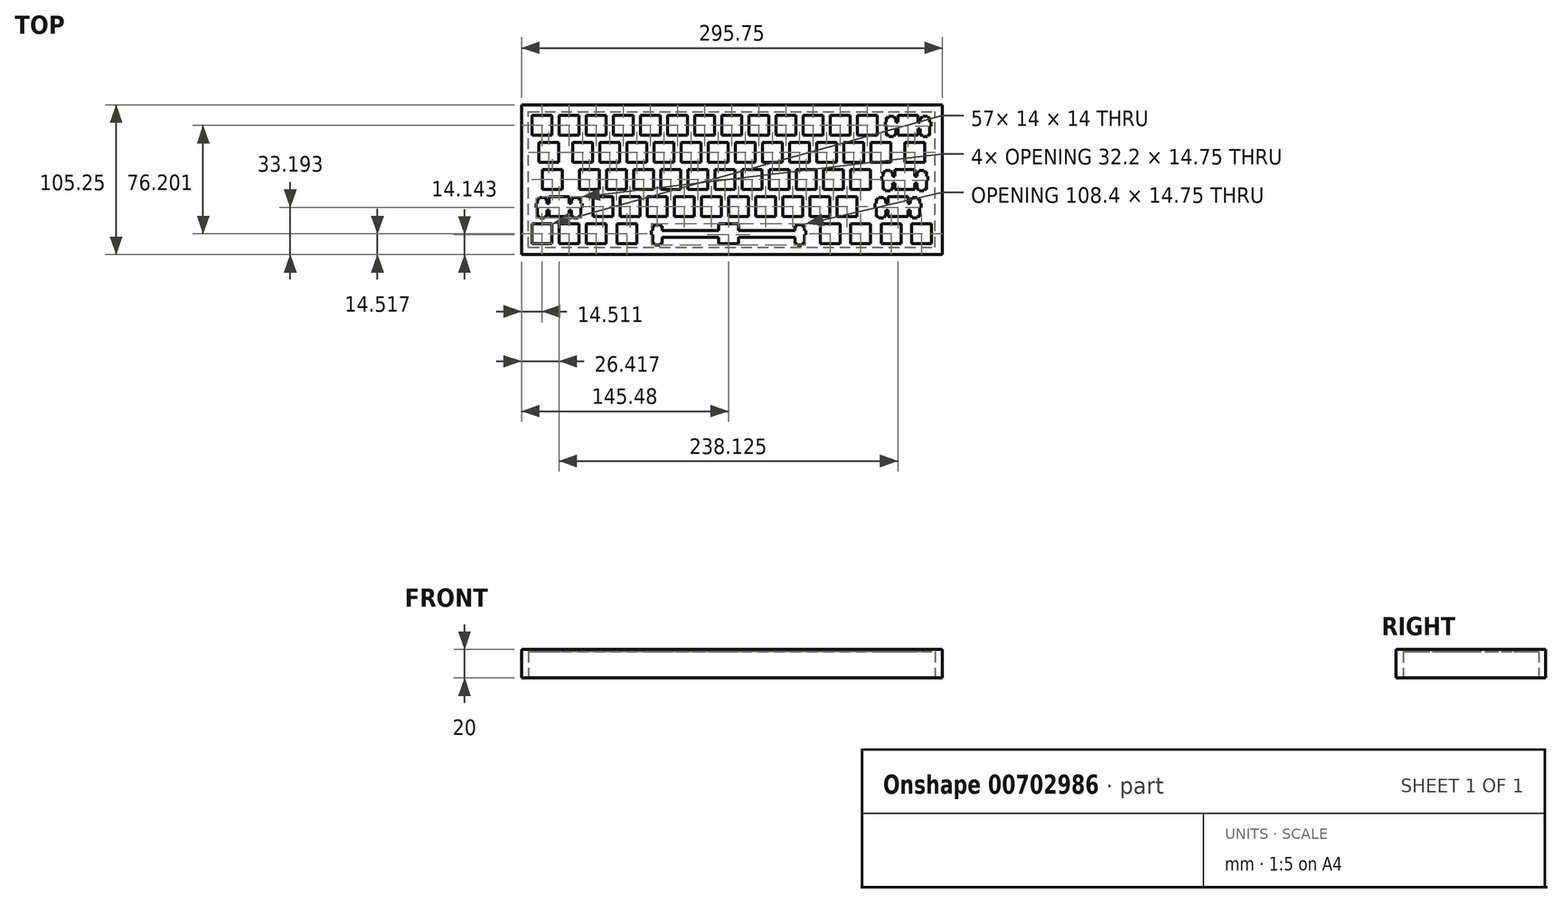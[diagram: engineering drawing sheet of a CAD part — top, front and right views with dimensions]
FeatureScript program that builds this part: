
annotation { "Feature Type Name" : "Feature", "Feature Type Description" : "" }
export const myFeature = defineFeature(function(context is Context, id is Id, definition is map)
    precondition{}
    {
        {
            var Q0;
            Q0=qCreatedBy(makeId("Top.planeOp"),FACE);
            var sketch = newSketch(context, id + "F0", { "sketchPlane" : qUnion([Q0])});
            skLineSegment(sketch, "E0.bottom", {"start": v(-142.74, 0) * mm, "end": v(153, 0) * mm});
            skLineSegment(sketch, "E0.top", {"start": v(-142.74, 105.25) * mm, "end": v(153, 105.25) * mm});
            skLineSegment(sketch, "E0.left", {"start": v(-142.74, 0) * mm, "end": v(-142.74, 105.25) * mm});
            skLineSegment(sketch, "E0.right", {"start": v(153, 0) * mm, "end": v(153, 105.25) * mm});
            skSolve(sketch);
        }
        {
            var Q0;
            Q0=makeQuery(id+"F0.imprint","IMPRINT",FACE,{"disambiguationData":[TD([[makeQuery(id+"F0.imprint","IMPRINT",EDGE,{"derivedFrom":sQuery(id+"F0.wireOp",EDGE,"E0.bottom")}),1.0]])]});
            extrude(context, id + "F1", {"entities" : qUnion([Q0]), "depth" : 20 * mm, "offsetDistance" : 25 * mm});
        }
        {
            var Q0;
            Q0=makeQuery(id+"F1.opExtrude","CAP_FACE",FACE,{"disambiguationData":[OSD([sQuery(id+"F0.wireOp",EDGE,"E0.bottom"),sQuery(id+"F0.wireOp",EDGE,"E0.top"),sQuery(id+"F0.wireOp",EDGE,"E0.left"),sQuery(id+"F0.wireOp",EDGE,"E0.right")])],"isStart":true});
            var sketch = newSketch(context, id + "F2", { "sketchPlane" : qUnion([Q0])});
            skLineSegment(sketch, "E1.bottom", {"start": v(-137.74, -5) * mm, "end": v(148, -5) * mm});
            skLineSegment(sketch, "E1.top", {"start": v(-137.74, -100.25) * mm, "end": v(148, -100.25) * mm});
            skLineSegment(sketch, "E1.left", {"start": v(-137.74, -5) * mm, "end": v(-137.74, -100.25) * mm});
            skLineSegment(sketch, "E1.right", {"start": v(148, -5) * mm, "end": v(148, -100.25) * mm});
            skSolve(sketch);
        }
        {
            var Q0;
            Q0=makeQuery(id+"F2.imprint","IMPRINT",FACE,{"disambiguationData":[TD([[makeQuery(id+"F2.imprint","IMPRINT",EDGE,{"derivedFrom":sQuery(id+"F2.wireOp",EDGE,"E1.bottom")}),-1.0]])]});
            extrude(context, id + "F3", {"entities" : qUnion([Q0]), "operationType" : NewBodyOperationType.REMOVE, "oppositeDirection" : true, "depth" : (20 - 1.54) * mm, "offsetDistance" : 25 * mm});
        }
        {
            var Q0;
            Q0=makeQuery(id+"F1.opExtrude","CAP_FACE",FACE,{"disambiguationData":[OSD([sQuery(id+"F0.wireOp",EDGE,"E0.bottom"),sQuery(id+"F0.wireOp",EDGE,"E0.top"),sQuery(id+"F0.wireOp",EDGE,"E0.left"),sQuery(id+"F0.wireOp",EDGE,"E0.right")])],"isStart":false});
            var sketch = newSketch(context, id + "F4", { "sketchPlane" : qUnion([Q0])});
            skLineSegment(sketch, "E2", {"start": v(-142.75, 105.24) * mm, "end": v(153, 105.24) * mm});
            skLineSegment(sketch, "E3", {"start": v(153, 105.24) * mm, "end": v(153, 0) * mm});
            skLineSegment(sketch, "E4", {"start": v(153, 0) * mm, "end": v(-142.75, 0) * mm});
            skLineSegment(sketch, "E5", {"start": v(-142.75, 0) * mm, "end": v(-142.75, 105.24) * mm});
            skLineSegment(sketch, "E6", {"start": v(-4.26, 21.52) * mm, "end": v(-4.26, 16.82) * mm});
            skLineSegment(sketch, "E7", {"start": v(-4.26, 16.82) * mm, "end": v(-43.88, 16.82) * mm});
            skLineSegment(sketch, "E8", {"start": v(-43.88, 16.82) * mm, "end": v(-43.88, 20.05) * mm});
            skLineSegment(sketch, "E9", {"start": v(-43.88, 20.05) * mm, "end": v(-45.6, 20.05) * mm});
            skLineSegment(sketch, "E10", {"start": v(-45.6, 20.05) * mm, "end": v(-45.6, 20.97) * mm});
            skLineSegment(sketch, "E11", {"start": v(-45.6, 20.97) * mm, "end": v(-48.91, 20.97) * mm});
            skLineSegment(sketch, "E12", {"start": v(-48.91, 20.97) * mm, "end": v(-48.91, 20.05) * mm});
            skLineSegment(sketch, "E13", {"start": v(-48.91, 20.05) * mm, "end": v(-50.64, 20.05) * mm});
            skLineSegment(sketch, "E14", {"start": v(-50.64, 20.05) * mm, "end": v(-50.64, 16.82) * mm});
            skLineSegment(sketch, "E15", {"start": v(-50.64, 16.82) * mm, "end": v(-51.46, 16.82) * mm});
            skLineSegment(sketch, "E16", {"start": v(-51.46, 16.82) * mm, "end": v(-51.46, 14.02) * mm});
            skLineSegment(sketch, "E17", {"start": v(-51.46, 14.02) * mm, "end": v(-50.64, 14.02) * mm});
            skLineSegment(sketch, "E18", {"start": v(-50.64, 14.02) * mm, "end": v(-50.64, 7.75) * mm});
            skLineSegment(sketch, "E19", {"start": v(-50.64, 7.75) * mm, "end": v(-48.91, 7.75) * mm});
            skLineSegment(sketch, "E20", {"start": v(-48.91, 7.75) * mm, "end": v(-48.91, 6.77) * mm});
            skLineSegment(sketch, "E21", {"start": v(-48.91, 6.77) * mm, "end": v(-45.6, 6.77) * mm});
            skLineSegment(sketch, "E22", {"start": v(-45.6, 6.77) * mm, "end": v(-45.6, 7.75) * mm});
            skLineSegment(sketch, "E23", {"start": v(-45.6, 7.75) * mm, "end": v(-43.88, 7.75) * mm});
            skLineSegment(sketch, "E24", {"start": v(-43.88, 7.75) * mm, "end": v(-43.88, 12.22) * mm});
            skLineSegment(sketch, "E25", {"start": v(-43.88, 12.22) * mm, "end": v(-4.26, 12.22) * mm});
            skLineSegment(sketch, "E26", {"start": v(-4.26, 12.22) * mm, "end": v(-4.26, 7.52) * mm});
            skLineSegment(sketch, "E27", {"start": v(-4.26, 7.52) * mm, "end": v(9.74, 7.52) * mm});
            skLineSegment(sketch, "E28", {"start": v(9.74, 7.52) * mm, "end": v(9.74, 12.22) * mm});
            skLineSegment(sketch, "E29", {"start": v(9.74, 12.22) * mm, "end": v(49.36, 12.22) * mm});
            skLineSegment(sketch, "E30", {"start": v(49.36, 12.22) * mm, "end": v(49.36, 7.75) * mm});
            skLineSegment(sketch, "E31", {"start": v(49.36, 7.75) * mm, "end": v(51.09, 7.75) * mm});
            skLineSegment(sketch, "E32", {"start": v(51.09, 7.75) * mm, "end": v(51.09, 6.77) * mm});
            skLineSegment(sketch, "E33", {"start": v(51.09, 6.77) * mm, "end": v(54.39, 6.77) * mm});
            skLineSegment(sketch, "E34", {"start": v(54.39, 6.77) * mm, "end": v(54.39, 7.75) * mm});
            skLineSegment(sketch, "E35", {"start": v(54.39, 7.75) * mm, "end": v(56.11, 7.75) * mm});
            skLineSegment(sketch, "E36", {"start": v(56.11, 7.75) * mm, "end": v(56.11, 14.02) * mm});
            skLineSegment(sketch, "E37", {"start": v(56.11, 14.02) * mm, "end": v(56.94, 14.02) * mm});
            skLineSegment(sketch, "E38", {"start": v(56.94, 14.02) * mm, "end": v(56.94, 16.82) * mm});
            skLineSegment(sketch, "E39", {"start": v(56.94, 16.82) * mm, "end": v(56.11, 16.82) * mm});
            skLineSegment(sketch, "E40", {"start": v(56.11, 16.82) * mm, "end": v(56.11, 20.05) * mm});
            skLineSegment(sketch, "E41", {"start": v(56.11, 20.05) * mm, "end": v(54.39, 20.05) * mm});
            skLineSegment(sketch, "E42", {"start": v(54.39, 20.05) * mm, "end": v(54.39, 20.97) * mm});
            skLineSegment(sketch, "E43", {"start": v(54.39, 20.97) * mm, "end": v(51.09, 20.97) * mm});
            skLineSegment(sketch, "E44", {"start": v(51.09, 20.97) * mm, "end": v(51.09, 20.05) * mm});
            skLineSegment(sketch, "E45", {"start": v(51.09, 20.05) * mm, "end": v(49.36, 20.05) * mm});
            skLineSegment(sketch, "E46", {"start": v(49.36, 20.05) * mm, "end": v(49.36, 16.82) * mm});
            skLineSegment(sketch, "E47", {"start": v(49.36, 16.82) * mm, "end": v(9.74, 16.82) * mm});
            skLineSegment(sketch, "E48", {"start": v(9.74, 16.82) * mm, "end": v(9.74, 21.52) * mm});
            skLineSegment(sketch, "E49", {"start": v(9.74, 21.52) * mm, "end": v(-4.26, 21.52) * mm});
            skLineSegment(sketch, "E50", {"start": v(-135.23, 21.52) * mm, "end": v(-121.23, 21.52) * mm});
            skLineSegment(sketch, "E51", {"start": v(-121.23, 21.52) * mm, "end": v(-121.23, 7.52) * mm});
            skLineSegment(sketch, "E52", {"start": v(-121.23, 7.52) * mm, "end": v(-135.23, 7.52) * mm});
            skLineSegment(sketch, "E53", {"start": v(-135.23, 7.52) * mm, "end": v(-135.23, 21.52) * mm});
            skLineSegment(sketch, "E54", {"start": v(-116.18, 21.52) * mm, "end": v(-102.18, 21.52) * mm});
            skLineSegment(sketch, "E55", {"start": v(-102.18, 21.52) * mm, "end": v(-102.18, 7.52) * mm});
            skLineSegment(sketch, "E56", {"start": v(-102.18, 7.52) * mm, "end": v(-116.18, 7.52) * mm});
            skLineSegment(sketch, "E57", {"start": v(-116.18, 7.52) * mm, "end": v(-116.18, 21.52) * mm});
            skLineSegment(sketch, "E58", {"start": v(-97.13, 21.52) * mm, "end": v(-83.13, 21.52) * mm});
            skLineSegment(sketch, "E59", {"start": v(-83.13, 21.52) * mm, "end": v(-83.13, 7.52) * mm});
            skLineSegment(sketch, "E60", {"start": v(-83.13, 7.52) * mm, "end": v(-97.13, 7.52) * mm});
            skLineSegment(sketch, "E61", {"start": v(-97.13, 7.52) * mm, "end": v(-97.13, 21.52) * mm});
            skLineSegment(sketch, "E62", {"start": v(-75.7, 21.52) * mm, "end": v(-61.7, 21.52) * mm});
            skLineSegment(sketch, "E63", {"start": v(-61.7, 21.52) * mm, "end": v(-61.7, 7.52) * mm});
            skLineSegment(sketch, "E64", {"start": v(-61.7, 7.52) * mm, "end": v(-75.7, 7.52) * mm});
            skLineSegment(sketch, "E65", {"start": v(-75.7, 7.52) * mm, "end": v(-75.7, 21.52) * mm});
            skLineSegment(sketch, "E66", {"start": v(67.18, 21.52) * mm, "end": v(81.18, 21.52) * mm});
            skLineSegment(sketch, "E67", {"start": v(81.18, 21.52) * mm, "end": v(81.18, 7.52) * mm});
            skLineSegment(sketch, "E68", {"start": v(81.18, 7.52) * mm, "end": v(67.18, 7.52) * mm});
            skLineSegment(sketch, "E69", {"start": v(67.18, 7.52) * mm, "end": v(67.18, 21.52) * mm});
            skLineSegment(sketch, "E70", {"start": v(88.6, 21.52) * mm, "end": v(102.6, 21.52) * mm});
            skLineSegment(sketch, "E71", {"start": v(102.6, 21.52) * mm, "end": v(102.6, 7.52) * mm});
            skLineSegment(sketch, "E72", {"start": v(102.6, 7.52) * mm, "end": v(88.6, 7.52) * mm});
            skLineSegment(sketch, "E73", {"start": v(88.6, 7.52) * mm, "end": v(88.6, 21.52) * mm});
            skLineSegment(sketch, "E74", {"start": v(110.04, 21.52) * mm, "end": v(124.04, 21.52) * mm});
            skLineSegment(sketch, "E75", {"start": v(124.04, 21.52) * mm, "end": v(124.04, 7.52) * mm});
            skLineSegment(sketch, "E76", {"start": v(124.04, 7.52) * mm, "end": v(110.04, 7.52) * mm});
            skLineSegment(sketch, "E77", {"start": v(110.04, 7.52) * mm, "end": v(110.04, 21.52) * mm});
            skLineSegment(sketch, "E78", {"start": v(131.47, 21.52) * mm, "end": v(145.47, 21.52) * mm});
            skLineSegment(sketch, "E79", {"start": v(145.47, 21.52) * mm, "end": v(145.47, 7.52) * mm});
            skLineSegment(sketch, "E80", {"start": v(145.47, 7.52) * mm, "end": v(131.47, 7.52) * mm});
            skLineSegment(sketch, "E81", {"start": v(131.47, 7.52) * mm, "end": v(131.47, 21.52) * mm});
            skLineSegment(sketch, "E82", {"start": v(-123.32, 40.57) * mm, "end": v(-123.32, 35.87) * mm});
            skLineSegment(sketch, "E83", {"start": v(-123.32, 35.87) * mm, "end": v(-124.85, 35.87) * mm});
            skLineSegment(sketch, "E84", {"start": v(-124.85, 35.87) * mm, "end": v(-124.85, 39.1) * mm});
            skLineSegment(sketch, "E85", {"start": v(-124.85, 39.1) * mm, "end": v(-126.57, 39.1) * mm});
            skLineSegment(sketch, "E86", {"start": v(-126.57, 39.1) * mm, "end": v(-126.57, 40.02) * mm});
            skLineSegment(sketch, "E87", {"start": v(-126.57, 40.02) * mm, "end": v(-129.87, 40.02) * mm});
            skLineSegment(sketch, "E88", {"start": v(-129.87, 40.02) * mm, "end": v(-129.87, 39.1) * mm});
            skLineSegment(sketch, "E89", {"start": v(-129.87, 39.1) * mm, "end": v(-131.6, 39.1) * mm});
            skLineSegment(sketch, "E90", {"start": v(-131.6, 39.1) * mm, "end": v(-131.6, 35.87) * mm});
            skLineSegment(sketch, "E91", {"start": v(-131.6, 35.87) * mm, "end": v(-132.42, 35.87) * mm});
            skLineSegment(sketch, "E92", {"start": v(-132.42, 35.87) * mm, "end": v(-132.42, 33.07) * mm});
            skLineSegment(sketch, "E93", {"start": v(-132.42, 33.07) * mm, "end": v(-131.6, 33.07) * mm});
            skLineSegment(sketch, "E94", {"start": v(-131.6, 33.07) * mm, "end": v(-131.6, 26.8) * mm});
            skLineSegment(sketch, "E95", {"start": v(-131.6, 26.8) * mm, "end": v(-129.87, 26.8) * mm});
            skLineSegment(sketch, "E96", {"start": v(-129.87, 26.8) * mm, "end": v(-129.87, 25.82) * mm});
            skLineSegment(sketch, "E97", {"start": v(-129.87, 25.82) * mm, "end": v(-126.57, 25.82) * mm});
            skLineSegment(sketch, "E98", {"start": v(-126.57, 25.82) * mm, "end": v(-126.57, 26.8) * mm});
            skLineSegment(sketch, "E99", {"start": v(-126.57, 26.8) * mm, "end": v(-124.85, 26.8) * mm});
            skLineSegment(sketch, "E100", {"start": v(-124.85, 26.8) * mm, "end": v(-124.85, 31.27) * mm});
            skLineSegment(sketch, "E101", {"start": v(-124.85, 31.27) * mm, "end": v(-123.32, 31.27) * mm});
            skLineSegment(sketch, "E102", {"start": v(-123.32, 31.27) * mm, "end": v(-123.32, 26.57) * mm});
            skLineSegment(sketch, "E103", {"start": v(-123.32, 26.57) * mm, "end": v(-109.32, 26.57) * mm});
            skLineSegment(sketch, "E104", {"start": v(-109.32, 26.57) * mm, "end": v(-109.32, 31.27) * mm});
            skLineSegment(sketch, "E105", {"start": v(-109.32, 31.27) * mm, "end": v(-107.8, 31.27) * mm});
            skLineSegment(sketch, "E106", {"start": v(-107.8, 31.27) * mm, "end": v(-107.8, 26.8) * mm});
            skLineSegment(sketch, "E107", {"start": v(-107.8, 26.8) * mm, "end": v(-106.07, 26.8) * mm});
            skLineSegment(sketch, "E108", {"start": v(-106.07, 26.8) * mm, "end": v(-106.07, 25.82) * mm});
            skLineSegment(sketch, "E109", {"start": v(-106.07, 25.82) * mm, "end": v(-102.77, 25.82) * mm});
            skLineSegment(sketch, "E110", {"start": v(-102.77, 25.82) * mm, "end": v(-102.77, 26.8) * mm});
            skLineSegment(sketch, "E111", {"start": v(-102.77, 26.8) * mm, "end": v(-101.05, 26.8) * mm});
            skLineSegment(sketch, "E112", {"start": v(-101.05, 26.8) * mm, "end": v(-101.05, 33.07) * mm});
            skLineSegment(sketch, "E113", {"start": v(-101.05, 33.07) * mm, "end": v(-100.22, 33.07) * mm});
            skLineSegment(sketch, "E114", {"start": v(-100.22, 33.07) * mm, "end": v(-100.22, 35.87) * mm});
            skLineSegment(sketch, "E115", {"start": v(-100.22, 35.87) * mm, "end": v(-101.05, 35.87) * mm});
            skLineSegment(sketch, "E116", {"start": v(-101.05, 35.87) * mm, "end": v(-101.05, 39.1) * mm});
            skLineSegment(sketch, "E117", {"start": v(-101.05, 39.1) * mm, "end": v(-102.77, 39.1) * mm});
            skLineSegment(sketch, "E118", {"start": v(-102.77, 39.1) * mm, "end": v(-102.77, 40.02) * mm});
            skLineSegment(sketch, "E119", {"start": v(-102.77, 40.02) * mm, "end": v(-106.07, 40.02) * mm});
            skLineSegment(sketch, "E120", {"start": v(-106.07, 40.02) * mm, "end": v(-106.07, 39.1) * mm});
            skLineSegment(sketch, "E121", {"start": v(-106.07, 39.1) * mm, "end": v(-107.8, 39.1) * mm});
            skLineSegment(sketch, "E122", {"start": v(-107.8, 39.1) * mm, "end": v(-107.8, 35.87) * mm});
            skLineSegment(sketch, "E123", {"start": v(-107.8, 35.87) * mm, "end": v(-109.32, 35.87) * mm});
            skLineSegment(sketch, "E124", {"start": v(-109.32, 35.87) * mm, "end": v(-109.32, 40.57) * mm});
            skLineSegment(sketch, "E125", {"start": v(-109.32, 40.57) * mm, "end": v(-123.32, 40.57) * mm});
            skLineSegment(sketch, "E126", {"start": v(114.8, 40.57) * mm, "end": v(114.8, 35.87) * mm});
            skLineSegment(sketch, "E127", {"start": v(114.8, 35.87) * mm, "end": v(113.28, 35.87) * mm});
            skLineSegment(sketch, "E128", {"start": v(113.28, 35.87) * mm, "end": v(113.28, 39.1) * mm});
            skLineSegment(sketch, "E129", {"start": v(113.28, 39.1) * mm, "end": v(111.55, 39.1) * mm});
            skLineSegment(sketch, "E130", {"start": v(111.55, 39.1) * mm, "end": v(111.55, 40.02) * mm});
            skLineSegment(sketch, "E131", {"start": v(111.55, 40.02) * mm, "end": v(108.25, 40.02) * mm});
            skLineSegment(sketch, "E132", {"start": v(108.25, 40.02) * mm, "end": v(108.25, 39.1) * mm});
            skLineSegment(sketch, "E133", {"start": v(108.25, 39.1) * mm, "end": v(106.53, 39.1) * mm});
            skLineSegment(sketch, "E134", {"start": v(106.53, 39.1) * mm, "end": v(106.53, 35.87) * mm});
            skLineSegment(sketch, "E135", {"start": v(106.53, 35.87) * mm, "end": v(105.7, 35.87) * mm});
            skLineSegment(sketch, "E136", {"start": v(105.7, 35.87) * mm, "end": v(105.7, 33.07) * mm});
            skLineSegment(sketch, "E137", {"start": v(105.7, 33.07) * mm, "end": v(106.53, 33.07) * mm});
            skLineSegment(sketch, "E138", {"start": v(106.53, 33.07) * mm, "end": v(106.53, 26.8) * mm});
            skLineSegment(sketch, "E139", {"start": v(106.53, 26.8) * mm, "end": v(108.25, 26.8) * mm});
            skLineSegment(sketch, "E140", {"start": v(108.25, 26.8) * mm, "end": v(108.25, 25.82) * mm});
            skLineSegment(sketch, "E141", {"start": v(108.25, 25.82) * mm, "end": v(111.55, 25.82) * mm});
            skLineSegment(sketch, "E142", {"start": v(111.55, 25.82) * mm, "end": v(111.55, 26.8) * mm});
            skLineSegment(sketch, "E143", {"start": v(111.55, 26.8) * mm, "end": v(113.28, 26.8) * mm});
            skLineSegment(sketch, "E144", {"start": v(113.28, 26.8) * mm, "end": v(113.28, 31.27) * mm});
            skLineSegment(sketch, "E145", {"start": v(113.28, 31.27) * mm, "end": v(114.8, 31.27) * mm});
            skLineSegment(sketch, "E146", {"start": v(114.8, 31.27) * mm, "end": v(114.8, 26.57) * mm});
            skLineSegment(sketch, "E147", {"start": v(114.8, 26.57) * mm, "end": v(128.8, 26.57) * mm});
            skLineSegment(sketch, "E148", {"start": v(128.8, 26.57) * mm, "end": v(128.8, 31.27) * mm});
            skLineSegment(sketch, "E149", {"start": v(128.8, 31.27) * mm, "end": v(130.33, 31.27) * mm});
            skLineSegment(sketch, "E150", {"start": v(130.33, 31.27) * mm, "end": v(130.33, 26.8) * mm});
            skLineSegment(sketch, "E151", {"start": v(130.33, 26.8) * mm, "end": v(132.05, 26.8) * mm});
            skLineSegment(sketch, "E152", {"start": v(132.05, 26.8) * mm, "end": v(132.05, 25.82) * mm});
            skLineSegment(sketch, "E153", {"start": v(132.05, 25.82) * mm, "end": v(135.35, 25.82) * mm});
            skLineSegment(sketch, "E154", {"start": v(135.35, 25.82) * mm, "end": v(135.35, 26.8) * mm});
            skLineSegment(sketch, "E155", {"start": v(135.35, 26.8) * mm, "end": v(137.08, 26.8) * mm});
            skLineSegment(sketch, "E156", {"start": v(137.08, 26.8) * mm, "end": v(137.08, 33.07) * mm});
            skLineSegment(sketch, "E157", {"start": v(137.08, 33.07) * mm, "end": v(137.9, 33.07) * mm});
            skLineSegment(sketch, "E158", {"start": v(137.9, 33.07) * mm, "end": v(137.9, 35.87) * mm});
            skLineSegment(sketch, "E159", {"start": v(137.9, 35.87) * mm, "end": v(137.08, 35.87) * mm});
            skLineSegment(sketch, "E160", {"start": v(137.08, 35.87) * mm, "end": v(137.08, 39.1) * mm});
            skLineSegment(sketch, "E161", {"start": v(137.08, 39.1) * mm, "end": v(135.35, 39.1) * mm});
            skLineSegment(sketch, "E162", {"start": v(135.35, 39.1) * mm, "end": v(135.35, 40.02) * mm});
            skLineSegment(sketch, "E163", {"start": v(135.35, 40.02) * mm, "end": v(132.05, 40.02) * mm});
            skLineSegment(sketch, "E164", {"start": v(132.05, 40.02) * mm, "end": v(132.05, 39.1) * mm});
            skLineSegment(sketch, "E165", {"start": v(132.05, 39.1) * mm, "end": v(130.33, 39.1) * mm});
            skLineSegment(sketch, "E166", {"start": v(130.33, 39.1) * mm, "end": v(130.33, 35.87) * mm});
            skLineSegment(sketch, "E167", {"start": v(130.33, 35.87) * mm, "end": v(128.8, 35.87) * mm});
            skLineSegment(sketch, "E168", {"start": v(128.8, 35.87) * mm, "end": v(128.8, 40.57) * mm});
            skLineSegment(sketch, "E169", {"start": v(128.8, 40.57) * mm, "end": v(114.8, 40.57) * mm});
            skLineSegment(sketch, "E170", {"start": v(-92.37, 40.57) * mm, "end": v(-78.37, 40.57) * mm});
            skLineSegment(sketch, "E171", {"start": v(-78.37, 40.57) * mm, "end": v(-78.37, 26.57) * mm});
            skLineSegment(sketch, "E172", {"start": v(-78.37, 26.57) * mm, "end": v(-92.37, 26.57) * mm});
            skLineSegment(sketch, "E173", {"start": v(-92.37, 26.57) * mm, "end": v(-92.37, 40.57) * mm});
            skLineSegment(sketch, "E174", {"start": v(-73.32, 40.57) * mm, "end": v(-59.32, 40.57) * mm});
            skLineSegment(sketch, "E175", {"start": v(-59.32, 40.57) * mm, "end": v(-59.32, 26.57) * mm});
            skLineSegment(sketch, "E176", {"start": v(-59.32, 26.57) * mm, "end": v(-73.32, 26.57) * mm});
            skLineSegment(sketch, "E177", {"start": v(-73.32, 26.57) * mm, "end": v(-73.32, 40.57) * mm});
            skLineSegment(sketch, "E178", {"start": v(-54.27, 40.57) * mm, "end": v(-40.27, 40.57) * mm});
            skLineSegment(sketch, "E179", {"start": v(-40.27, 40.57) * mm, "end": v(-40.27, 26.57) * mm});
            skLineSegment(sketch, "E180", {"start": v(-40.27, 26.57) * mm, "end": v(-54.27, 26.57) * mm});
            skLineSegment(sketch, "E181", {"start": v(-54.27, 26.57) * mm, "end": v(-54.27, 40.57) * mm});
            skLineSegment(sketch, "E182", {"start": v(-35.22, 40.57) * mm, "end": v(-21.22, 40.57) * mm});
            skLineSegment(sketch, "E183", {"start": v(-21.22, 40.57) * mm, "end": v(-21.22, 26.57) * mm});
            skLineSegment(sketch, "E184", {"start": v(-21.22, 26.57) * mm, "end": v(-35.22, 26.57) * mm});
            skLineSegment(sketch, "E185", {"start": v(-35.22, 26.57) * mm, "end": v(-35.22, 40.57) * mm});
            skLineSegment(sketch, "E186", {"start": v(-16.17, 40.57) * mm, "end": v(-2.17, 40.57) * mm});
            skLineSegment(sketch, "E187", {"start": v(-2.17, 40.57) * mm, "end": v(-2.17, 26.57) * mm});
            skLineSegment(sketch, "E188", {"start": v(-2.17, 26.57) * mm, "end": v(-16.17, 26.57) * mm});
            skLineSegment(sketch, "E189", {"start": v(-16.17, 26.57) * mm, "end": v(-16.17, 40.57) * mm});
            skLineSegment(sketch, "E190", {"start": v(2.88, 40.57) * mm, "end": v(16.88, 40.57) * mm});
            skLineSegment(sketch, "E191", {"start": v(16.88, 40.57) * mm, "end": v(16.88, 26.57) * mm});
            skLineSegment(sketch, "E192", {"start": v(16.88, 26.57) * mm, "end": v(2.88, 26.57) * mm});
            skLineSegment(sketch, "E193", {"start": v(2.88, 26.57) * mm, "end": v(2.88, 40.57) * mm});
            skLineSegment(sketch, "E194", {"start": v(21.93, 40.57) * mm, "end": v(35.93, 40.57) * mm});
            skLineSegment(sketch, "E195", {"start": v(35.93, 40.57) * mm, "end": v(35.93, 26.57) * mm});
            skLineSegment(sketch, "E196", {"start": v(35.93, 26.57) * mm, "end": v(21.93, 26.57) * mm});
            skLineSegment(sketch, "E197", {"start": v(21.93, 26.57) * mm, "end": v(21.93, 40.57) * mm});
            skLineSegment(sketch, "E198", {"start": v(40.98, 40.57) * mm, "end": v(54.98, 40.57) * mm});
            skLineSegment(sketch, "E199", {"start": v(54.98, 40.57) * mm, "end": v(54.98, 26.57) * mm});
            skLineSegment(sketch, "E200", {"start": v(54.98, 26.57) * mm, "end": v(40.98, 26.57) * mm});
            skLineSegment(sketch, "E201", {"start": v(40.98, 26.57) * mm, "end": v(40.98, 40.57) * mm});
            skLineSegment(sketch, "E202", {"start": v(60.03, 40.57) * mm, "end": v(74.03, 40.57) * mm});
            skLineSegment(sketch, "E203", {"start": v(74.03, 40.57) * mm, "end": v(74.03, 26.57) * mm});
            skLineSegment(sketch, "E204", {"start": v(74.03, 26.57) * mm, "end": v(60.03, 26.57) * mm});
            skLineSegment(sketch, "E205", {"start": v(60.03, 26.57) * mm, "end": v(60.03, 40.57) * mm});
            skLineSegment(sketch, "E206", {"start": v(79.08, 40.57) * mm, "end": v(93.08, 40.57) * mm});
            skLineSegment(sketch, "E207", {"start": v(93.08, 40.57) * mm, "end": v(93.08, 26.57) * mm});
            skLineSegment(sketch, "E208", {"start": v(93.08, 26.57) * mm, "end": v(79.08, 26.57) * mm});
            skLineSegment(sketch, "E209", {"start": v(79.08, 26.57) * mm, "end": v(79.08, 40.57) * mm});
            skLineSegment(sketch, "E210", {"start": v(119.56, 59.62) * mm, "end": v(119.56, 54.92) * mm});
            skLineSegment(sketch, "E211", {"start": v(119.56, 54.92) * mm, "end": v(118.04, 54.92) * mm});
            skLineSegment(sketch, "E212", {"start": v(118.04, 54.92) * mm, "end": v(118.04, 58.15) * mm});
            skLineSegment(sketch, "E213", {"start": v(118.04, 58.15) * mm, "end": v(116.31, 58.15) * mm});
            skLineSegment(sketch, "E214", {"start": v(116.31, 58.15) * mm, "end": v(116.31, 59.07) * mm});
            skLineSegment(sketch, "E215", {"start": v(116.31, 59.07) * mm, "end": v(113.01, 59.07) * mm});
            skLineSegment(sketch, "E216", {"start": v(113.01, 59.07) * mm, "end": v(113.01, 58.15) * mm});
            skLineSegment(sketch, "E217", {"start": v(113.01, 58.15) * mm, "end": v(111.29, 58.15) * mm});
            skLineSegment(sketch, "E218", {"start": v(111.29, 58.15) * mm, "end": v(111.29, 54.92) * mm});
            skLineSegment(sketch, "E219", {"start": v(111.29, 54.92) * mm, "end": v(110.46, 54.92) * mm});
            skLineSegment(sketch, "E220", {"start": v(110.46, 54.92) * mm, "end": v(110.46, 52.12) * mm});
            skLineSegment(sketch, "E221", {"start": v(110.46, 52.12) * mm, "end": v(111.29, 52.12) * mm});
            skLineSegment(sketch, "E222", {"start": v(111.29, 52.12) * mm, "end": v(111.29, 45.85) * mm});
            skLineSegment(sketch, "E223", {"start": v(111.29, 45.85) * mm, "end": v(113.01, 45.85) * mm});
            skLineSegment(sketch, "E224", {"start": v(113.01, 45.85) * mm, "end": v(113.01, 44.87) * mm});
            skLineSegment(sketch, "E225", {"start": v(113.01, 44.87) * mm, "end": v(116.31, 44.87) * mm});
            skLineSegment(sketch, "E226", {"start": v(116.31, 44.87) * mm, "end": v(116.31, 45.85) * mm});
            skLineSegment(sketch, "E227", {"start": v(116.31, 45.85) * mm, "end": v(118.04, 45.85) * mm});
            skLineSegment(sketch, "E228", {"start": v(118.04, 45.85) * mm, "end": v(118.04, 50.32) * mm});
            skLineSegment(sketch, "E229", {"start": v(118.04, 50.32) * mm, "end": v(119.56, 50.32) * mm});
            skLineSegment(sketch, "E230", {"start": v(119.56, 50.32) * mm, "end": v(119.56, 45.62) * mm});
            skLineSegment(sketch, "E231", {"start": v(119.56, 45.62) * mm, "end": v(133.56, 45.62) * mm});
            skLineSegment(sketch, "E232", {"start": v(133.56, 45.62) * mm, "end": v(133.56, 50.32) * mm});
            skLineSegment(sketch, "E233", {"start": v(133.56, 50.32) * mm, "end": v(135.09, 50.32) * mm});
            skLineSegment(sketch, "E234", {"start": v(135.09, 50.32) * mm, "end": v(135.09, 45.85) * mm});
            skLineSegment(sketch, "E235", {"start": v(135.09, 45.85) * mm, "end": v(136.81, 45.85) * mm});
            skLineSegment(sketch, "E236", {"start": v(136.81, 45.85) * mm, "end": v(136.81, 44.87) * mm});
            skLineSegment(sketch, "E237", {"start": v(136.81, 44.87) * mm, "end": v(140.11, 44.87) * mm});
            skLineSegment(sketch, "E238", {"start": v(140.11, 44.87) * mm, "end": v(140.11, 45.85) * mm});
            skLineSegment(sketch, "E239", {"start": v(140.11, 45.85) * mm, "end": v(141.84, 45.85) * mm});
            skLineSegment(sketch, "E240", {"start": v(141.84, 45.85) * mm, "end": v(141.84, 52.12) * mm});
            skLineSegment(sketch, "E241", {"start": v(141.84, 52.12) * mm, "end": v(142.66, 52.12) * mm});
            skLineSegment(sketch, "E242", {"start": v(142.66, 52.12) * mm, "end": v(142.66, 54.92) * mm});
            skLineSegment(sketch, "E243", {"start": v(142.66, 54.92) * mm, "end": v(141.84, 54.92) * mm});
            skLineSegment(sketch, "E244", {"start": v(141.84, 54.92) * mm, "end": v(141.84, 58.15) * mm});
            skLineSegment(sketch, "E245", {"start": v(141.84, 58.15) * mm, "end": v(140.11, 58.15) * mm});
            skLineSegment(sketch, "E246", {"start": v(140.11, 58.15) * mm, "end": v(140.11, 59.07) * mm});
            skLineSegment(sketch, "E247", {"start": v(140.11, 59.07) * mm, "end": v(136.81, 59.07) * mm});
            skLineSegment(sketch, "E248", {"start": v(136.81, 59.07) * mm, "end": v(136.81, 58.15) * mm});
            skLineSegment(sketch, "E249", {"start": v(136.81, 58.15) * mm, "end": v(135.09, 58.15) * mm});
            skLineSegment(sketch, "E250", {"start": v(135.09, 58.15) * mm, "end": v(135.09, 54.92) * mm});
            skLineSegment(sketch, "E251", {"start": v(135.09, 54.92) * mm, "end": v(133.56, 54.92) * mm});
            skLineSegment(sketch, "E252", {"start": v(133.56, 54.92) * mm, "end": v(133.56, 59.62) * mm});
            skLineSegment(sketch, "E253", {"start": v(133.56, 59.62) * mm, "end": v(119.56, 59.62) * mm});
            skLineSegment(sketch, "E254", {"start": v(-128.09, 59.62) * mm, "end": v(-114.08, 59.62) * mm});
            skLineSegment(sketch, "E255", {"start": v(-114.08, 59.62) * mm, "end": v(-114.08, 45.62) * mm});
            skLineSegment(sketch, "E256", {"start": v(-114.08, 45.62) * mm, "end": v(-128.09, 45.62) * mm});
            skLineSegment(sketch, "E257", {"start": v(-128.09, 45.62) * mm, "end": v(-128.09, 59.62) * mm});
            skLineSegment(sketch, "E258", {"start": v(-101.9, 59.62) * mm, "end": v(-87.9, 59.62) * mm});
            skLineSegment(sketch, "E259", {"start": v(-87.9, 59.62) * mm, "end": v(-87.9, 45.62) * mm});
            skLineSegment(sketch, "E260", {"start": v(-87.9, 45.62) * mm, "end": v(-101.9, 45.62) * mm});
            skLineSegment(sketch, "E261", {"start": v(-101.9, 45.62) * mm, "end": v(-101.9, 59.62) * mm});
            skLineSegment(sketch, "E262", {"start": v(-82.84, 59.62) * mm, "end": v(-68.84, 59.62) * mm});
            skLineSegment(sketch, "E263", {"start": v(-68.84, 59.62) * mm, "end": v(-68.84, 45.62) * mm});
            skLineSegment(sketch, "E264", {"start": v(-68.84, 45.62) * mm, "end": v(-82.84, 45.62) * mm});
            skLineSegment(sketch, "E265", {"start": v(-82.84, 45.62) * mm, "end": v(-82.84, 59.62) * mm});
            skLineSegment(sketch, "E266", {"start": v(-63.8, 59.62) * mm, "end": v(-49.8, 59.62) * mm});
            skLineSegment(sketch, "E267", {"start": v(-49.8, 59.62) * mm, "end": v(-49.8, 45.62) * mm});
            skLineSegment(sketch, "E268", {"start": v(-49.8, 45.62) * mm, "end": v(-63.8, 45.62) * mm});
            skLineSegment(sketch, "E269", {"start": v(-63.8, 45.62) * mm, "end": v(-63.8, 59.62) * mm});
            skLineSegment(sketch, "E270", {"start": v(-44.74, 59.62) * mm, "end": v(-30.74, 59.62) * mm});
            skLineSegment(sketch, "E271", {"start": v(-30.74, 59.62) * mm, "end": v(-30.74, 45.62) * mm});
            skLineSegment(sketch, "E272", {"start": v(-30.74, 45.62) * mm, "end": v(-44.74, 45.62) * mm});
            skLineSegment(sketch, "E273", {"start": v(-44.74, 45.62) * mm, "end": v(-44.74, 59.62) * mm});
            skLineSegment(sketch, "E274", {"start": v(-25.7, 59.62) * mm, "end": v(-11.7, 59.62) * mm});
            skLineSegment(sketch, "E275", {"start": v(-11.7, 59.62) * mm, "end": v(-11.7, 45.62) * mm});
            skLineSegment(sketch, "E276", {"start": v(-11.7, 45.62) * mm, "end": v(-25.7, 45.62) * mm});
            skLineSegment(sketch, "E277", {"start": v(-25.7, 45.62) * mm, "end": v(-25.7, 59.62) * mm});
            skLineSegment(sketch, "E278", {"start": v(-6.64, 59.62) * mm, "end": v(7.36, 59.62) * mm});
            skLineSegment(sketch, "E279", {"start": v(7.36, 59.62) * mm, "end": v(7.36, 45.62) * mm});
            skLineSegment(sketch, "E280", {"start": v(7.36, 45.62) * mm, "end": v(-6.64, 45.62) * mm});
            skLineSegment(sketch, "E281", {"start": v(-6.64, 45.62) * mm, "end": v(-6.64, 59.62) * mm});
            skLineSegment(sketch, "E282", {"start": v(12.4, 59.62) * mm, "end": v(26.4, 59.62) * mm});
            skLineSegment(sketch, "E283", {"start": v(26.4, 59.62) * mm, "end": v(26.4, 45.62) * mm});
            skLineSegment(sketch, "E284", {"start": v(26.4, 45.62) * mm, "end": v(12.4, 45.62) * mm});
            skLineSegment(sketch, "E285", {"start": v(12.4, 45.62) * mm, "end": v(12.4, 59.62) * mm});
            skLineSegment(sketch, "E286", {"start": v(31.46, 59.62) * mm, "end": v(45.46, 59.62) * mm});
            skLineSegment(sketch, "E287", {"start": v(45.46, 59.62) * mm, "end": v(45.46, 45.62) * mm});
            skLineSegment(sketch, "E288", {"start": v(45.46, 45.62) * mm, "end": v(31.46, 45.62) * mm});
            skLineSegment(sketch, "E289", {"start": v(31.46, 45.62) * mm, "end": v(31.46, 59.62) * mm});
            skLineSegment(sketch, "E290", {"start": v(50.5, 59.62) * mm, "end": v(64.5, 59.62) * mm});
            skLineSegment(sketch, "E291", {"start": v(64.5, 59.62) * mm, "end": v(64.5, 45.62) * mm});
            skLineSegment(sketch, "E292", {"start": v(64.5, 45.62) * mm, "end": v(50.5, 45.62) * mm});
            skLineSegment(sketch, "E293", {"start": v(50.5, 45.62) * mm, "end": v(50.5, 59.62) * mm});
            skLineSegment(sketch, "E294", {"start": v(69.56, 59.62) * mm, "end": v(83.56, 59.62) * mm});
            skLineSegment(sketch, "E295", {"start": v(83.56, 59.62) * mm, "end": v(83.56, 45.62) * mm});
            skLineSegment(sketch, "E296", {"start": v(83.56, 45.62) * mm, "end": v(69.56, 45.62) * mm});
            skLineSegment(sketch, "E297", {"start": v(69.56, 45.62) * mm, "end": v(69.56, 59.62) * mm});
            skLineSegment(sketch, "E298", {"start": v(88.6, 59.62) * mm, "end": v(102.6, 59.62) * mm});
            skLineSegment(sketch, "E299", {"start": v(102.6, 59.62) * mm, "end": v(102.6, 45.62) * mm});
            skLineSegment(sketch, "E300", {"start": v(102.6, 45.62) * mm, "end": v(88.6, 45.62) * mm});
            skLineSegment(sketch, "E301", {"start": v(88.6, 45.62) * mm, "end": v(88.6, 59.62) * mm});
            skLineSegment(sketch, "E302", {"start": v(-130.47, 78.67) * mm, "end": v(-116.47, 78.67) * mm});
            skLineSegment(sketch, "E303", {"start": v(-116.47, 78.67) * mm, "end": v(-116.47, 64.67) * mm});
            skLineSegment(sketch, "E304", {"start": v(-116.47, 64.67) * mm, "end": v(-130.47, 64.67) * mm});
            skLineSegment(sketch, "E305", {"start": v(-130.47, 64.67) * mm, "end": v(-130.47, 78.67) * mm});
            skLineSegment(sketch, "E306", {"start": v(-106.65, 78.67) * mm, "end": v(-92.65, 78.67) * mm});
            skLineSegment(sketch, "E307", {"start": v(-92.65, 78.67) * mm, "end": v(-92.65, 64.67) * mm});
            skLineSegment(sketch, "E308", {"start": v(-92.65, 64.67) * mm, "end": v(-106.65, 64.67) * mm});
            skLineSegment(sketch, "E309", {"start": v(-106.65, 64.67) * mm, "end": v(-106.65, 78.67) * mm});
            skLineSegment(sketch, "E310", {"start": v(-87.6, 78.67) * mm, "end": v(-73.6, 78.67) * mm});
            skLineSegment(sketch, "E311", {"start": v(-73.6, 78.67) * mm, "end": v(-73.6, 64.67) * mm});
            skLineSegment(sketch, "E312", {"start": v(-73.6, 64.67) * mm, "end": v(-87.6, 64.67) * mm});
            skLineSegment(sketch, "E313", {"start": v(-87.6, 64.67) * mm, "end": v(-87.6, 78.67) * mm});
            skLineSegment(sketch, "E314", {"start": v(-68.55, 78.67) * mm, "end": v(-54.55, 78.67) * mm});
            skLineSegment(sketch, "E315", {"start": v(-54.55, 78.67) * mm, "end": v(-54.55, 64.67) * mm});
            skLineSegment(sketch, "E316", {"start": v(-54.55, 64.67) * mm, "end": v(-68.55, 64.67) * mm});
            skLineSegment(sketch, "E317", {"start": v(-68.55, 64.67) * mm, "end": v(-68.55, 78.67) * mm});
            skLineSegment(sketch, "E318", {"start": v(-49.5, 78.67) * mm, "end": v(-35.5, 78.67) * mm});
            skLineSegment(sketch, "E319", {"start": v(-35.5, 78.67) * mm, "end": v(-35.5, 64.67) * mm});
            skLineSegment(sketch, "E320", {"start": v(-35.5, 64.67) * mm, "end": v(-49.5, 64.67) * mm});
            skLineSegment(sketch, "E321", {"start": v(-49.5, 64.67) * mm, "end": v(-49.5, 78.67) * mm});
            skLineSegment(sketch, "E322", {"start": v(-30.45, 78.67) * mm, "end": v(-16.45, 78.67) * mm});
            skLineSegment(sketch, "E323", {"start": v(-16.45, 78.67) * mm, "end": v(-16.45, 64.67) * mm});
            skLineSegment(sketch, "E324", {"start": v(-16.45, 64.67) * mm, "end": v(-30.45, 64.67) * mm});
            skLineSegment(sketch, "E325", {"start": v(-30.45, 64.67) * mm, "end": v(-30.45, 78.67) * mm});
            skLineSegment(sketch, "E326", {"start": v(-11.4, 78.67) * mm, "end": v(2.6, 78.67) * mm});
            skLineSegment(sketch, "E327", {"start": v(2.6, 78.67) * mm, "end": v(2.6, 64.67) * mm});
            skLineSegment(sketch, "E328", {"start": v(2.6, 64.67) * mm, "end": v(-11.4, 64.67) * mm});
            skLineSegment(sketch, "E329", {"start": v(-11.4, 64.67) * mm, "end": v(-11.4, 78.67) * mm});
            skLineSegment(sketch, "E330", {"start": v(7.65, 78.67) * mm, "end": v(21.65, 78.67) * mm});
            skLineSegment(sketch, "E331", {"start": v(21.65, 78.67) * mm, "end": v(21.65, 64.67) * mm});
            skLineSegment(sketch, "E332", {"start": v(21.65, 64.67) * mm, "end": v(7.65, 64.67) * mm});
            skLineSegment(sketch, "E333", {"start": v(7.65, 64.67) * mm, "end": v(7.65, 78.67) * mm});
            skLineSegment(sketch, "E334", {"start": v(26.7, 78.67) * mm, "end": v(40.7, 78.67) * mm});
            skLineSegment(sketch, "E335", {"start": v(40.7, 78.67) * mm, "end": v(40.7, 64.67) * mm});
            skLineSegment(sketch, "E336", {"start": v(40.7, 64.67) * mm, "end": v(26.7, 64.67) * mm});
            skLineSegment(sketch, "E337", {"start": v(26.7, 64.67) * mm, "end": v(26.7, 78.67) * mm});
            skLineSegment(sketch, "E338", {"start": v(45.75, 78.67) * mm, "end": v(59.75, 78.67) * mm});
            skLineSegment(sketch, "E339", {"start": v(59.75, 78.67) * mm, "end": v(59.75, 64.67) * mm});
            skLineSegment(sketch, "E340", {"start": v(59.75, 64.67) * mm, "end": v(45.75, 64.67) * mm});
            skLineSegment(sketch, "E341", {"start": v(45.75, 64.67) * mm, "end": v(45.75, 78.67) * mm});
            skLineSegment(sketch, "E342", {"start": v(64.8, 78.67) * mm, "end": v(78.8, 78.67) * mm});
            skLineSegment(sketch, "E343", {"start": v(78.8, 78.67) * mm, "end": v(78.8, 64.67) * mm});
            skLineSegment(sketch, "E344", {"start": v(78.8, 64.67) * mm, "end": v(64.8, 64.67) * mm});
            skLineSegment(sketch, "E345", {"start": v(64.8, 64.67) * mm, "end": v(64.8, 78.67) * mm});
            skLineSegment(sketch, "E346", {"start": v(83.85, 78.67) * mm, "end": v(97.85, 78.67) * mm});
            skLineSegment(sketch, "E347", {"start": v(97.85, 78.67) * mm, "end": v(97.85, 64.67) * mm});
            skLineSegment(sketch, "E348", {"start": v(97.85, 64.67) * mm, "end": v(83.85, 64.67) * mm});
            skLineSegment(sketch, "E349", {"start": v(83.85, 64.67) * mm, "end": v(83.85, 78.67) * mm});
            skLineSegment(sketch, "E350", {"start": v(102.9, 78.67) * mm, "end": v(116.9, 78.67) * mm});
            skLineSegment(sketch, "E351", {"start": v(116.9, 78.67) * mm, "end": v(116.9, 64.67) * mm});
            skLineSegment(sketch, "E352", {"start": v(116.9, 64.67) * mm, "end": v(102.9, 64.67) * mm});
            skLineSegment(sketch, "E353", {"start": v(102.9, 64.67) * mm, "end": v(102.9, 78.67) * mm});
            skLineSegment(sketch, "E354", {"start": v(126.7, 78.67) * mm, "end": v(140.7, 78.67) * mm});
            skLineSegment(sketch, "E355", {"start": v(140.7, 78.67) * mm, "end": v(140.7, 64.67) * mm});
            skLineSegment(sketch, "E356", {"start": v(140.7, 64.67) * mm, "end": v(126.7, 64.67) * mm});
            skLineSegment(sketch, "E357", {"start": v(126.7, 64.67) * mm, "end": v(126.7, 78.67) * mm});
            skLineSegment(sketch, "E358", {"start": v(121.95, 97.72) * mm, "end": v(121.95, 93.02) * mm});
            skLineSegment(sketch, "E359", {"start": v(121.95, 93.02) * mm, "end": v(120.42, 93.02) * mm});
            skLineSegment(sketch, "E360", {"start": v(120.42, 93.02) * mm, "end": v(120.42, 96.25) * mm});
            skLineSegment(sketch, "E361", {"start": v(120.42, 96.25) * mm, "end": v(118.7, 96.25) * mm});
            skLineSegment(sketch, "E362", {"start": v(118.7, 96.25) * mm, "end": v(118.7, 97.17) * mm});
            skLineSegment(sketch, "E363", {"start": v(118.7, 97.17) * mm, "end": v(115.4, 97.17) * mm});
            skLineSegment(sketch, "E364", {"start": v(115.4, 97.17) * mm, "end": v(115.4, 96.25) * mm});
            skLineSegment(sketch, "E365", {"start": v(115.4, 96.25) * mm, "end": v(113.67, 96.25) * mm});
            skLineSegment(sketch, "E366", {"start": v(113.67, 96.25) * mm, "end": v(113.67, 93.02) * mm});
            skLineSegment(sketch, "E367", {"start": v(113.67, 93.02) * mm, "end": v(112.85, 93.02) * mm});
            skLineSegment(sketch, "E368", {"start": v(112.85, 93.02) * mm, "end": v(112.85, 90.22) * mm});
            skLineSegment(sketch, "E369", {"start": v(112.85, 90.22) * mm, "end": v(113.67, 90.22) * mm});
            skLineSegment(sketch, "E370", {"start": v(113.67, 90.22) * mm, "end": v(113.67, 83.95) * mm});
            skLineSegment(sketch, "E371", {"start": v(113.67, 83.95) * mm, "end": v(115.4, 83.95) * mm});
            skLineSegment(sketch, "E372", {"start": v(115.4, 83.95) * mm, "end": v(115.4, 82.97) * mm});
            skLineSegment(sketch, "E373", {"start": v(115.4, 82.97) * mm, "end": v(118.7, 82.97) * mm});
            skLineSegment(sketch, "E374", {"start": v(118.7, 82.97) * mm, "end": v(118.7, 83.95) * mm});
            skLineSegment(sketch, "E375", {"start": v(118.7, 83.95) * mm, "end": v(120.42, 83.95) * mm});
            skLineSegment(sketch, "E376", {"start": v(120.42, 83.95) * mm, "end": v(120.42, 88.42) * mm});
            skLineSegment(sketch, "E377", {"start": v(120.42, 88.42) * mm, "end": v(121.95, 88.42) * mm});
            skLineSegment(sketch, "E378", {"start": v(121.95, 88.42) * mm, "end": v(121.95, 83.72) * mm});
            skLineSegment(sketch, "E379", {"start": v(121.95, 83.72) * mm, "end": v(135.95, 83.72) * mm});
            skLineSegment(sketch, "E380", {"start": v(135.95, 83.72) * mm, "end": v(135.95, 88.42) * mm});
            skLineSegment(sketch, "E381", {"start": v(135.95, 88.42) * mm, "end": v(137.47, 88.42) * mm});
            skLineSegment(sketch, "E382", {"start": v(137.47, 88.42) * mm, "end": v(137.47, 83.95) * mm});
            skLineSegment(sketch, "E383", {"start": v(137.47, 83.95) * mm, "end": v(139.2, 83.95) * mm});
            skLineSegment(sketch, "E384", {"start": v(139.2, 83.95) * mm, "end": v(139.2, 82.97) * mm});
            skLineSegment(sketch, "E385", {"start": v(139.2, 82.97) * mm, "end": v(142.5, 82.97) * mm});
            skLineSegment(sketch, "E386", {"start": v(142.5, 82.97) * mm, "end": v(142.5, 83.95) * mm});
            skLineSegment(sketch, "E387", {"start": v(142.5, 83.95) * mm, "end": v(144.22, 83.95) * mm});
            skLineSegment(sketch, "E388", {"start": v(144.22, 83.95) * mm, "end": v(144.22, 90.22) * mm});
            skLineSegment(sketch, "E389", {"start": v(144.22, 90.22) * mm, "end": v(145.05, 90.22) * mm});
            skLineSegment(sketch, "E390", {"start": v(145.05, 90.22) * mm, "end": v(145.05, 93.02) * mm});
            skLineSegment(sketch, "E391", {"start": v(145.05, 93.02) * mm, "end": v(144.22, 93.02) * mm});
            skLineSegment(sketch, "E392", {"start": v(144.22, 93.02) * mm, "end": v(144.22, 96.25) * mm});
            skLineSegment(sketch, "E393", {"start": v(144.22, 96.25) * mm, "end": v(142.5, 96.25) * mm});
            skLineSegment(sketch, "E394", {"start": v(142.5, 96.25) * mm, "end": v(142.5, 97.17) * mm});
            skLineSegment(sketch, "E395", {"start": v(142.5, 97.17) * mm, "end": v(139.2, 97.17) * mm});
            skLineSegment(sketch, "E396", {"start": v(139.2, 97.17) * mm, "end": v(139.2, 96.25) * mm});
            skLineSegment(sketch, "E397", {"start": v(139.2, 96.25) * mm, "end": v(137.47, 96.25) * mm});
            skLineSegment(sketch, "E398", {"start": v(137.47, 96.25) * mm, "end": v(137.47, 93.02) * mm});
            skLineSegment(sketch, "E399", {"start": v(137.47, 93.02) * mm, "end": v(135.95, 93.02) * mm});
            skLineSegment(sketch, "E400", {"start": v(135.95, 93.02) * mm, "end": v(135.95, 97.72) * mm});
            skLineSegment(sketch, "E401", {"start": v(135.95, 97.72) * mm, "end": v(121.95, 97.72) * mm});
            skLineSegment(sketch, "E402", {"start": v(-135.23, 97.72) * mm, "end": v(-121.23, 97.72) * mm});
            skLineSegment(sketch, "E403", {"start": v(-121.23, 97.72) * mm, "end": v(-121.23, 83.72) * mm});
            skLineSegment(sketch, "E404", {"start": v(-121.23, 83.72) * mm, "end": v(-135.23, 83.72) * mm});
            skLineSegment(sketch, "E405", {"start": v(-135.23, 83.72) * mm, "end": v(-135.23, 97.72) * mm});
            skLineSegment(sketch, "E406", {"start": v(-116.18, 97.72) * mm, "end": v(-102.18, 97.72) * mm});
            skLineSegment(sketch, "E407", {"start": v(-102.18, 97.72) * mm, "end": v(-102.18, 83.72) * mm});
            skLineSegment(sketch, "E408", {"start": v(-102.18, 83.72) * mm, "end": v(-116.18, 83.72) * mm});
            skLineSegment(sketch, "E409", {"start": v(-116.18, 83.72) * mm, "end": v(-116.18, 97.72) * mm});
            skLineSegment(sketch, "E410", {"start": v(-97.13, 97.72) * mm, "end": v(-83.13, 97.72) * mm});
            skLineSegment(sketch, "E411", {"start": v(-83.13, 97.72) * mm, "end": v(-83.13, 83.72) * mm});
            skLineSegment(sketch, "E412", {"start": v(-83.13, 83.72) * mm, "end": v(-97.13, 83.72) * mm});
            skLineSegment(sketch, "E413", {"start": v(-97.13, 83.72) * mm, "end": v(-97.13, 97.72) * mm});
            skLineSegment(sketch, "E414", {"start": v(-78.08, 97.72) * mm, "end": v(-64.08, 97.72) * mm});
            skLineSegment(sketch, "E415", {"start": v(-64.08, 97.72) * mm, "end": v(-64.08, 83.72) * mm});
            skLineSegment(sketch, "E416", {"start": v(-64.08, 83.72) * mm, "end": v(-78.08, 83.72) * mm});
            skLineSegment(sketch, "E417", {"start": v(-78.08, 83.72) * mm, "end": v(-78.08, 97.72) * mm});
            skLineSegment(sketch, "E418", {"start": v(-59.03, 97.72) * mm, "end": v(-45.03, 97.72) * mm});
            skLineSegment(sketch, "E419", {"start": v(-45.03, 97.72) * mm, "end": v(-45.03, 83.72) * mm});
            skLineSegment(sketch, "E420", {"start": v(-45.03, 83.72) * mm, "end": v(-59.03, 83.72) * mm});
            skLineSegment(sketch, "E421", {"start": v(-59.03, 83.72) * mm, "end": v(-59.03, 97.72) * mm});
            skLineSegment(sketch, "E422", {"start": v(-39.98, 97.72) * mm, "end": v(-25.98, 97.72) * mm});
            skLineSegment(sketch, "E423", {"start": v(-25.98, 97.72) * mm, "end": v(-25.98, 83.72) * mm});
            skLineSegment(sketch, "E424", {"start": v(-25.98, 83.72) * mm, "end": v(-39.98, 83.72) * mm});
            skLineSegment(sketch, "E425", {"start": v(-39.98, 83.72) * mm, "end": v(-39.98, 97.72) * mm});
            skLineSegment(sketch, "E426", {"start": v(-20.93, 97.72) * mm, "end": v(-6.93, 97.72) * mm});
            skLineSegment(sketch, "E427", {"start": v(-6.93, 97.72) * mm, "end": v(-6.93, 83.72) * mm});
            skLineSegment(sketch, "E428", {"start": v(-6.93, 83.72) * mm, "end": v(-20.93, 83.72) * mm});
            skLineSegment(sketch, "E429", {"start": v(-20.93, 83.72) * mm, "end": v(-20.93, 97.72) * mm});
            skLineSegment(sketch, "E430", {"start": v(-1.88, 97.72) * mm, "end": v(12.12, 97.72) * mm});
            skLineSegment(sketch, "E431", {"start": v(12.12, 97.72) * mm, "end": v(12.12, 83.72) * mm});
            skLineSegment(sketch, "E432", {"start": v(12.12, 83.72) * mm, "end": v(-1.88, 83.72) * mm});
            skLineSegment(sketch, "E433", {"start": v(-1.88, 83.72) * mm, "end": v(-1.88, 97.72) * mm});
            skLineSegment(sketch, "E434", {"start": v(17.17, 97.72) * mm, "end": v(31.17, 97.72) * mm});
            skLineSegment(sketch, "E435", {"start": v(31.17, 97.72) * mm, "end": v(31.17, 83.72) * mm});
            skLineSegment(sketch, "E436", {"start": v(31.17, 83.72) * mm, "end": v(17.17, 83.72) * mm});
            skLineSegment(sketch, "E437", {"start": v(17.17, 83.72) * mm, "end": v(17.17, 97.72) * mm});
            skLineSegment(sketch, "E438", {"start": v(36.22, 97.72) * mm, "end": v(50.22, 97.72) * mm});
            skLineSegment(sketch, "E439", {"start": v(50.22, 97.72) * mm, "end": v(50.22, 83.72) * mm});
            skLineSegment(sketch, "E440", {"start": v(50.22, 83.72) * mm, "end": v(36.22, 83.72) * mm});
            skLineSegment(sketch, "E441", {"start": v(36.22, 83.72) * mm, "end": v(36.22, 97.72) * mm});
            skLineSegment(sketch, "E442", {"start": v(55.27, 97.72) * mm, "end": v(69.27, 97.72) * mm});
            skLineSegment(sketch, "E443", {"start": v(69.27, 97.72) * mm, "end": v(69.27, 83.72) * mm});
            skLineSegment(sketch, "E444", {"start": v(69.27, 83.72) * mm, "end": v(55.27, 83.72) * mm});
            skLineSegment(sketch, "E445", {"start": v(55.27, 83.72) * mm, "end": v(55.27, 97.72) * mm});
            skLineSegment(sketch, "E446", {"start": v(74.32, 97.72) * mm, "end": v(88.32, 97.72) * mm});
            skLineSegment(sketch, "E447", {"start": v(88.32, 97.72) * mm, "end": v(88.32, 83.72) * mm});
            skLineSegment(sketch, "E448", {"start": v(88.32, 83.72) * mm, "end": v(74.32, 83.72) * mm});
            skLineSegment(sketch, "E449", {"start": v(74.32, 83.72) * mm, "end": v(74.32, 97.72) * mm});
            skLineSegment(sketch, "E450", {"start": v(93.37, 97.72) * mm, "end": v(107.37, 97.72) * mm});
            skLineSegment(sketch, "E451", {"start": v(107.37, 97.72) * mm, "end": v(107.37, 83.72) * mm});
            skLineSegment(sketch, "E452", {"start": v(107.37, 83.72) * mm, "end": v(93.37, 83.72) * mm});
            skLineSegment(sketch, "E453", {"start": v(93.37, 83.72) * mm, "end": v(93.37, 97.72) * mm});
            skSolve(sketch);
        }
        {
            var Q0;
            Q0=makeQuery(id+"F4.imprint","IMPRINT",FACE,{"disambiguationData":[TD([[makeQuery(id+"F4.imprint","IMPRINT",EDGE,{"derivedFrom":sQuery(id+"F4.wireOp",EDGE,"E402")}),-1.0]])]});
            var Q1;
            Q1=makeQuery(id+"F4.imprint","IMPRINT",FACE,{"disambiguationData":[TD([[makeQuery(id+"F4.imprint","IMPRINT",EDGE,{"derivedFrom":sQuery(id+"F4.wireOp",EDGE,"E406")}),-1.0]])]});
            var Q2;
            Q2=makeQuery(id+"F4.imprint","IMPRINT",FACE,{"disambiguationData":[TD([[makeQuery(id+"F4.imprint","IMPRINT",EDGE,{"derivedFrom":sQuery(id+"F4.wireOp",EDGE,"E410")}),-1.0]])]});
            var Q3;
            Q3=makeQuery(id+"F4.imprint","IMPRINT",FACE,{"disambiguationData":[TD([[makeQuery(id+"F4.imprint","IMPRINT",EDGE,{"derivedFrom":sQuery(id+"F4.wireOp",EDGE,"E414")}),-1.0]])]});
            var Q4;
            Q4=makeQuery(id+"F4.imprint","IMPRINT",FACE,{"disambiguationData":[TD([[makeQuery(id+"F4.imprint","IMPRINT",EDGE,{"derivedFrom":sQuery(id+"F4.wireOp",EDGE,"E418")}),-1.0]])]});
            var Q5;
            Q5=makeQuery(id+"F4.imprint","IMPRINT",FACE,{"disambiguationData":[TD([[makeQuery(id+"F4.imprint","IMPRINT",EDGE,{"derivedFrom":sQuery(id+"F4.wireOp",EDGE,"E422")}),-1.0]])]});
            var Q6;
            Q6=makeQuery(id+"F4.imprint","IMPRINT",FACE,{"disambiguationData":[TD([[makeQuery(id+"F4.imprint","IMPRINT",EDGE,{"derivedFrom":sQuery(id+"F4.wireOp",EDGE,"E426")}),-1.0]])]});
            var Q7;
            Q7=makeQuery(id+"F4.imprint","IMPRINT",FACE,{"disambiguationData":[TD([[makeQuery(id+"F4.imprint","IMPRINT",EDGE,{"derivedFrom":sQuery(id+"F4.wireOp",EDGE,"E430")}),-1.0]])]});
            var Q8;
            Q8=makeQuery(id+"F4.imprint","IMPRINT",FACE,{"disambiguationData":[TD([[makeQuery(id+"F4.imprint","IMPRINT",EDGE,{"derivedFrom":sQuery(id+"F4.wireOp",EDGE,"E434")}),-1.0]])]});
            var Q9;
            Q9=makeQuery(id+"F4.imprint","IMPRINT",FACE,{"disambiguationData":[TD([[makeQuery(id+"F4.imprint","IMPRINT",EDGE,{"derivedFrom":sQuery(id+"F4.wireOp",EDGE,"E438")}),-1.0]])]});
            var Q10;
            Q10=makeQuery(id+"F4.imprint","IMPRINT",FACE,{"disambiguationData":[TD([[makeQuery(id+"F4.imprint","IMPRINT",EDGE,{"derivedFrom":sQuery(id+"F4.wireOp",EDGE,"E442")}),-1.0]])]});
            var Q11;
            Q11=makeQuery(id+"F4.imprint","IMPRINT",FACE,{"disambiguationData":[TD([[makeQuery(id+"F4.imprint","IMPRINT",EDGE,{"derivedFrom":sQuery(id+"F4.wireOp",EDGE,"E446")}),-1.0]])]});
            var Q12;
            Q12=makeQuery(id+"F4.imprint","IMPRINT",FACE,{"disambiguationData":[TD([[makeQuery(id+"F4.imprint","IMPRINT",EDGE,{"derivedFrom":sQuery(id+"F4.wireOp",EDGE,"E450")}),-1.0]])]});
            var Q13;
            Q13=makeQuery(id+"F4.imprint","IMPRINT",FACE,{"disambiguationData":[TD([[makeQuery(id+"F4.imprint","IMPRINT",EDGE,{"derivedFrom":sQuery(id+"F4.wireOp",EDGE,"E358")}),1.0]])]});
            var Q14;
            Q14=makeQuery(id+"F4.imprint","IMPRINT",FACE,{"disambiguationData":[TD([[makeQuery(id+"F4.imprint","IMPRINT",EDGE,{"derivedFrom":sQuery(id+"F4.wireOp",EDGE,"E354")}),-1.0]])]});
            var Q15;
            Q15=makeQuery(id+"F4.imprint","IMPRINT",FACE,{"disambiguationData":[TD([[makeQuery(id+"F4.imprint","IMPRINT",EDGE,{"derivedFrom":sQuery(id+"F4.wireOp",EDGE,"E350")}),-1.0]])]});
            var Q16;
            Q16=makeQuery(id+"F4.imprint","IMPRINT",FACE,{"disambiguationData":[TD([[makeQuery(id+"F4.imprint","IMPRINT",EDGE,{"derivedFrom":sQuery(id+"F4.wireOp",EDGE,"E302")}),-1.0]])]});
            var Q17;
            Q17=makeQuery(id+"F4.imprint","IMPRINT",FACE,{"disambiguationData":[TD([[makeQuery(id+"F4.imprint","IMPRINT",EDGE,{"derivedFrom":sQuery(id+"F4.wireOp",EDGE,"E306")}),-1.0]])]});
            var Q18;
            Q18=makeQuery(id+"F4.imprint","IMPRINT",FACE,{"disambiguationData":[TD([[makeQuery(id+"F4.imprint","IMPRINT",EDGE,{"derivedFrom":sQuery(id+"F4.wireOp",EDGE,"E310")}),-1.0]])]});
            var Q19;
            Q19=makeQuery(id+"F4.imprint","IMPRINT",FACE,{"disambiguationData":[TD([[makeQuery(id+"F4.imprint","IMPRINT",EDGE,{"derivedFrom":sQuery(id+"F4.wireOp",EDGE,"E314")}),-1.0]])]});
            var Q20;
            Q20=makeQuery(id+"F4.imprint","IMPRINT",FACE,{"disambiguationData":[TD([[makeQuery(id+"F4.imprint","IMPRINT",EDGE,{"derivedFrom":sQuery(id+"F4.wireOp",EDGE,"E318")}),-1.0]])]});
            var Q21;
            Q21=makeQuery(id+"F4.imprint","IMPRINT",FACE,{"disambiguationData":[TD([[makeQuery(id+"F4.imprint","IMPRINT",EDGE,{"derivedFrom":sQuery(id+"F4.wireOp",EDGE,"E322")}),-1.0]])]});
            var Q22;
            Q22=makeQuery(id+"F4.imprint","IMPRINT",FACE,{"disambiguationData":[TD([[makeQuery(id+"F4.imprint","IMPRINT",EDGE,{"derivedFrom":sQuery(id+"F4.wireOp",EDGE,"E326")}),-1.0]])]});
            var Q23;
            Q23=makeQuery(id+"F4.imprint","IMPRINT",FACE,{"disambiguationData":[TD([[makeQuery(id+"F4.imprint","IMPRINT",EDGE,{"derivedFrom":sQuery(id+"F4.wireOp",EDGE,"E330")}),-1.0]])]});
            var Q24;
            Q24=makeQuery(id+"F4.imprint","IMPRINT",FACE,{"disambiguationData":[TD([[makeQuery(id+"F4.imprint","IMPRINT",EDGE,{"derivedFrom":sQuery(id+"F4.wireOp",EDGE,"E334")}),-1.0]])]});
            var Q25;
            Q25=makeQuery(id+"F4.imprint","IMPRINT",FACE,{"disambiguationData":[TD([[makeQuery(id+"F4.imprint","IMPRINT",EDGE,{"derivedFrom":sQuery(id+"F4.wireOp",EDGE,"E338")}),-1.0]])]});
            var Q26;
            Q26=makeQuery(id+"F4.imprint","IMPRINT",FACE,{"disambiguationData":[TD([[makeQuery(id+"F4.imprint","IMPRINT",EDGE,{"derivedFrom":sQuery(id+"F4.wireOp",EDGE,"E342")}),-1.0]])]});
            var Q27;
            Q27=makeQuery(id+"F4.imprint","IMPRINT",FACE,{"disambiguationData":[TD([[makeQuery(id+"F4.imprint","IMPRINT",EDGE,{"derivedFrom":sQuery(id+"F4.wireOp",EDGE,"E346")}),-1.0]])]});
            var Q28;
            Q28=makeQuery(id+"F4.imprint","IMPRINT",FACE,{"disambiguationData":[TD([[makeQuery(id+"F4.imprint","IMPRINT",EDGE,{"derivedFrom":sQuery(id+"F4.wireOp",EDGE,"E210")}),1.0]])]});
            var Q29;
            Q29=makeQuery(id+"F4.imprint","IMPRINT",FACE,{"disambiguationData":[TD([[makeQuery(id+"F4.imprint","IMPRINT",EDGE,{"derivedFrom":sQuery(id+"F4.wireOp",EDGE,"E294")}),-1.0]])]});
            var Q30;
            Q30=makeQuery(id+"F4.imprint","IMPRINT",FACE,{"disambiguationData":[TD([[makeQuery(id+"F4.imprint","IMPRINT",EDGE,{"derivedFrom":sQuery(id+"F4.wireOp",EDGE,"E290")}),-1.0]])]});
            var Q31;
            Q31=makeQuery(id+"F4.imprint","IMPRINT",FACE,{"disambiguationData":[TD([[makeQuery(id+"F4.imprint","IMPRINT",EDGE,{"derivedFrom":sQuery(id+"F4.wireOp",EDGE,"E286")}),-1.0]])]});
            var Q32;
            Q32=makeQuery(id+"F4.imprint","IMPRINT",FACE,{"disambiguationData":[TD([[makeQuery(id+"F4.imprint","IMPRINT",EDGE,{"derivedFrom":sQuery(id+"F4.wireOp",EDGE,"E282")}),-1.0]])]});
            var Q33;
            Q33=makeQuery(id+"F4.imprint","IMPRINT",FACE,{"disambiguationData":[TD([[makeQuery(id+"F4.imprint","IMPRINT",EDGE,{"derivedFrom":sQuery(id+"F4.wireOp",EDGE,"E278")}),-1.0]])]});
            var Q34;
            Q34=makeQuery(id+"F4.imprint","IMPRINT",FACE,{"disambiguationData":[TD([[makeQuery(id+"F4.imprint","IMPRINT",EDGE,{"derivedFrom":sQuery(id+"F4.wireOp",EDGE,"E274")}),-1.0]])]});
            var Q35;
            Q35=makeQuery(id+"F4.imprint","IMPRINT",FACE,{"disambiguationData":[TD([[makeQuery(id+"F4.imprint","IMPRINT",EDGE,{"derivedFrom":sQuery(id+"F4.wireOp",EDGE,"E298")}),-1.0]])]});
            var Q36;
            Q36=makeQuery(id+"F4.imprint","IMPRINT",FACE,{"disambiguationData":[TD([[makeQuery(id+"F4.imprint","IMPRINT",EDGE,{"derivedFrom":sQuery(id+"F4.wireOp",EDGE,"E254")}),-1.0]])]});
            var Q37;
            Q37=makeQuery(id+"F4.imprint","IMPRINT",FACE,{"disambiguationData":[TD([[makeQuery(id+"F4.imprint","IMPRINT",EDGE,{"derivedFrom":sQuery(id+"F4.wireOp",EDGE,"E82")}),1.0]])]});
            var Q38;
            Q38=makeQuery(id+"F4.imprint","IMPRINT",FACE,{"disambiguationData":[TD([[makeQuery(id+"F4.imprint","IMPRINT",EDGE,{"derivedFrom":sQuery(id+"F4.wireOp",EDGE,"E170")}),-1.0]])]});
            var Q39;
            Q39=makeQuery(id+"F4.imprint","IMPRINT",FACE,{"disambiguationData":[TD([[makeQuery(id+"F4.imprint","IMPRINT",EDGE,{"derivedFrom":sQuery(id+"F4.wireOp",EDGE,"E174")}),-1.0]])]});
            var Q40;
            Q40=makeQuery(id+"F4.imprint","IMPRINT",FACE,{"disambiguationData":[TD([[makeQuery(id+"F4.imprint","IMPRINT",EDGE,{"derivedFrom":sQuery(id+"F4.wireOp",EDGE,"E258")}),-1.0]])]});
            var Q41;
            Q41=makeQuery(id+"F4.imprint","IMPRINT",FACE,{"disambiguationData":[TD([[makeQuery(id+"F4.imprint","IMPRINT",EDGE,{"derivedFrom":sQuery(id+"F4.wireOp",EDGE,"E262")}),-1.0]])]});
            var Q42;
            Q42=makeQuery(id+"F4.imprint","IMPRINT",FACE,{"disambiguationData":[TD([[makeQuery(id+"F4.imprint","IMPRINT",EDGE,{"derivedFrom":sQuery(id+"F4.wireOp",EDGE,"E266")}),-1.0]])]});
            var Q43;
            Q43=makeQuery(id+"F4.imprint","IMPRINT",FACE,{"disambiguationData":[TD([[makeQuery(id+"F4.imprint","IMPRINT",EDGE,{"derivedFrom":sQuery(id+"F4.wireOp",EDGE,"E270")}),-1.0]])]});
            var Q44;
            Q44=makeQuery(id+"F4.imprint","IMPRINT",FACE,{"disambiguationData":[TD([[makeQuery(id+"F4.imprint","IMPRINT",EDGE,{"derivedFrom":sQuery(id+"F4.wireOp",EDGE,"E178")}),-1.0]])]});
            var Q45;
            Q45=makeQuery(id+"F4.imprint","IMPRINT",FACE,{"disambiguationData":[TD([[makeQuery(id+"F4.imprint","IMPRINT",EDGE,{"derivedFrom":sQuery(id+"F4.wireOp",EDGE,"E182")}),-1.0]])]});
            var Q46;
            Q46=makeQuery(id+"F4.imprint","IMPRINT",FACE,{"disambiguationData":[TD([[makeQuery(id+"F4.imprint","IMPRINT",EDGE,{"derivedFrom":sQuery(id+"F4.wireOp",EDGE,"E186")}),-1.0]])]});
            var Q47;
            Q47=makeQuery(id+"F4.imprint","IMPRINT",FACE,{"disambiguationData":[TD([[makeQuery(id+"F4.imprint","IMPRINT",EDGE,{"derivedFrom":sQuery(id+"F4.wireOp",EDGE,"E190")}),-1.0]])]});
            var Q48;
            Q48=makeQuery(id+"F4.imprint","IMPRINT",FACE,{"disambiguationData":[TD([[makeQuery(id+"F4.imprint","IMPRINT",EDGE,{"derivedFrom":sQuery(id+"F4.wireOp",EDGE,"E194")}),-1.0]])]});
            var Q49;
            Q49=makeQuery(id+"F4.imprint","IMPRINT",FACE,{"disambiguationData":[TD([[makeQuery(id+"F4.imprint","IMPRINT",EDGE,{"derivedFrom":sQuery(id+"F4.wireOp",EDGE,"E198")}),-1.0]])]});
            var Q50;
            Q50=makeQuery(id+"F4.imprint","IMPRINT",FACE,{"disambiguationData":[TD([[makeQuery(id+"F4.imprint","IMPRINT",EDGE,{"derivedFrom":sQuery(id+"F4.wireOp",EDGE,"E202")}),-1.0]])]});
            var Q51;
            Q51=makeQuery(id+"F4.imprint","IMPRINT",FACE,{"disambiguationData":[TD([[makeQuery(id+"F4.imprint","IMPRINT",EDGE,{"derivedFrom":sQuery(id+"F4.wireOp",EDGE,"E206")}),-1.0]])]});
            var Q52;
            Q52=makeQuery(id+"F4.imprint","IMPRINT",FACE,{"disambiguationData":[TD([[makeQuery(id+"F4.imprint","IMPRINT",EDGE,{"derivedFrom":sQuery(id+"F4.wireOp",EDGE,"E126")}),1.0]])]});
            var Q53;
            Q53=makeQuery(id+"F4.imprint","IMPRINT",FACE,{"disambiguationData":[TD([[makeQuery(id+"F4.imprint","IMPRINT",EDGE,{"derivedFrom":sQuery(id+"F4.wireOp",EDGE,"E74")}),-1.0]])]});
            var Q54;
            Q54=makeQuery(id+"F4.imprint","IMPRINT",FACE,{"disambiguationData":[TD([[makeQuery(id+"F4.imprint","IMPRINT",EDGE,{"derivedFrom":sQuery(id+"F4.wireOp",EDGE,"E70")}),-1.0]])]});
            var Q55;
            Q55=makeQuery(id+"F4.imprint","IMPRINT",FACE,{"disambiguationData":[TD([[makeQuery(id+"F4.imprint","IMPRINT",EDGE,{"derivedFrom":sQuery(id+"F4.wireOp",EDGE,"E66")}),-1.0]])]});
            var Q56;
            Q56=makeQuery(id+"F4.imprint","IMPRINT",FACE,{"disambiguationData":[TD([[makeQuery(id+"F4.imprint","IMPRINT",EDGE,{"derivedFrom":sQuery(id+"F4.wireOp",EDGE,"E78")}),-1.0]])]});
            var Q57;
            Q57=makeQuery(id+"F4.imprint","IMPRINT",FACE,{"disambiguationData":[TD([[makeQuery(id+"F4.imprint","IMPRINT",EDGE,{"derivedFrom":sQuery(id+"F4.wireOp",EDGE,"E6")}),1.0]])]});
            var Q58;
            Q58=makeQuery(id+"F4.imprint","IMPRINT",FACE,{"disambiguationData":[TD([[makeQuery(id+"F4.imprint","IMPRINT",EDGE,{"derivedFrom":sQuery(id+"F4.wireOp",EDGE,"E50")}),-1.0]])]});
            var Q59;
            Q59=makeQuery(id+"F4.imprint","IMPRINT",FACE,{"disambiguationData":[TD([[makeQuery(id+"F4.imprint","IMPRINT",EDGE,{"derivedFrom":sQuery(id+"F4.wireOp",EDGE,"E54")}),-1.0]])]});
            var Q60;
            Q60=makeQuery(id+"F4.imprint","IMPRINT",FACE,{"disambiguationData":[TD([[makeQuery(id+"F4.imprint","IMPRINT",EDGE,{"derivedFrom":sQuery(id+"F4.wireOp",EDGE,"E58")}),-1.0]])]});
            var Q61;
            Q61=makeQuery(id+"F4.imprint","IMPRINT",FACE,{"disambiguationData":[TD([[makeQuery(id+"F4.imprint","IMPRINT",EDGE,{"derivedFrom":sQuery(id+"F4.wireOp",EDGE,"E62")}),-1.0]])]});
            extrude(context, id + "F5", {"entities" : qUnion([Q0, Q1, Q2, Q3, Q4, Q5, Q6, Q7, Q8, Q9, Q10, Q11, Q12, Q13, Q14, Q15, Q16, Q17, Q18, Q19, Q20, Q21, Q22, Q23, Q24, Q25, Q26, Q27, Q28, Q29, Q30, Q31, Q32, Q33, Q34, Q35, Q36, Q37, Q38, Q39, Q40, Q41, Q42, Q43, Q44, Q45, Q46, Q47, Q48, Q49, Q50, Q51, Q52, Q53, Q54, Q55, Q56, Q57, Q58, Q59, Q60, Q61]), "operationType" : NewBodyOperationType.REMOVE, "endBound" : BoundingType.THROUGH_ALL, "oppositeDirection" : true, "depth" : 50 * mm, "offsetDistance" : 25 * mm});
        }
        {
            var Q0;
            Q0=makeQuery(id+"F1.opExtrude","SWEPT_BODY",BODY,{"disambiguationData":[OSD([sQuery(id+"F0.wireOp",EDGE,"E0.bottom"),sQuery(id+"F0.wireOp",EDGE,"E0.top"),sQuery(id+"F0.wireOp",EDGE,"E0.left"),sQuery(id+"F0.wireOp",EDGE,"E0.right")])]});
            transform(context, id + "F6", {"entities" : qUnion([Q0]), "transformType" : TransformType.TRANSLATION_3D, "dx" : 0 * mm, "dy" : -(105 / 2) * mm, "dz" : 0 * mm, "makeCopy" : false});
        }
    });
